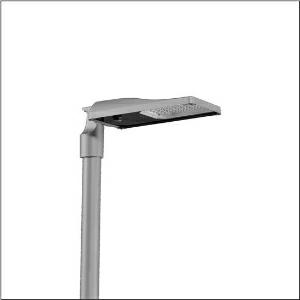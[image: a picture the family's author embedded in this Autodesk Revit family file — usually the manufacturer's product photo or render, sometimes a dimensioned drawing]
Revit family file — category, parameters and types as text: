
# Revit family: streetlight_sl_31_mini___st1_0a_5xh6d3ar08ja_50f1
name_source: partatom
category: Lighting Fixtures
units: mm (PartAtom-declared; Revit-internal decimal feet)

## family parameters
Cut with Voids When Loaded = No
Host = Face
Light Source = No
Part Type = Normal
Room Calculation Point = No
Round Connector Dimension = Use Diameter
Shared = No

## types (1)
- --- (1 x LED, 12270 lm, 82.5 W, 3000K)
    Apparent Load = 83 VA
    CIE Flux Codes = 40 73 97 100 100
    Color Rendering = 70
    Color Temperature = 3000K
    Default Elevation = 1800 mm
    Description = Streetlight SL 31 mini D4i mast luminaire for post-top, side-entry; light control with lens of PMMA; light distribution: ST1.0a, direct asymmetric distribution, for standard-compliant lighting for roads and squares; LED: luminous flux: 12.270lm, light colour: 730, colour temperature: 3000K; luminous efficacy: 148,7lm/W; control: pre-setting: logarithmic dimming characteristic, flexible luminous flux parameterisation, time-dependent luminous flux control, constant luminous flux control, power reduction, intelligent temperature release in ECG and LED module, overheat protection; luminaire housing, of diecast aluminium, SITECO metallic grey (DB 702S), corrosivity category C5 high according to DIN EN ISO 12944; cover of toughened safety glass, transparent, opened without tools; mast flange of diecast aluminium, SITECO metallic grey (DB 702S), spigot size: 76/60mm, mast flange included unmounted; cable length: 10,5m, connection cable pre-assembled; mains connection: 220..240V, AC, 50/60Hz; power consumption (at start of service life): 82,5W / (at end of service life): 90,1W / (with reduced operation 50%): 36,8W; protection rating (complete): IP66; insulation class (complete): insulation class II (safety insulation); impact resistance: IK09; certification: CE, ENEC, ENEC+, VDE, UKCA, ZD4i; permissible operating ambient temperature for outdoor applications: -40..+50°C; packaging unit: 1 piece

Light Distribution: ST1.0a
    Height = 76 mm
    Lamp = 1 x LED
    Lamp Light Flux = 12270 lm
    Lamp Power = 82.5 W
    Lamp count = 1
    Length = 547 mm
    Luminous efficacy = 149 lm/W
    Manufacturer = Siteco
    ModVariant = No
    Model = 5XH6D3AR08JA
    Number of Poles = 1
    OnlyDefault = Yes
    Power Factor = 1
    Product Name = Streetlight SL 31 mini | ST1.0a
    Product group = mast luminaire | pylon top
    ProductGroupID = 6100
    Protection Class = Protection class II
    Protection Degree = IP 66
    RLX_Detail_Level = 1
    RLX_Emergency_Light_Flux = 0 lm
    RLX_Emergency_Type = 0
    RLX_Emergency_Type_DB = No
    RlxData = <blob elided: 39665 chars, md5=bc7ce896>
    Socket = socket
    Standby Power = 0 W
    System Light Flux = 12270 lm
    System Power = 83 W
    Type Comments = factory setting: luminous flux: 100 % | dim-lin: 254 | 870 mA
    Type Image = l_1300328.jpg
    URL = http://relux.com
    VarID = @adj_057195
    Voltage = 0 V
    Weight = 0.00 kg
    Width = 265 mm

## geometry (parser evidence)
native form markers: Blend x4, Sweep x9
no freeform markers — native parametric forms only
